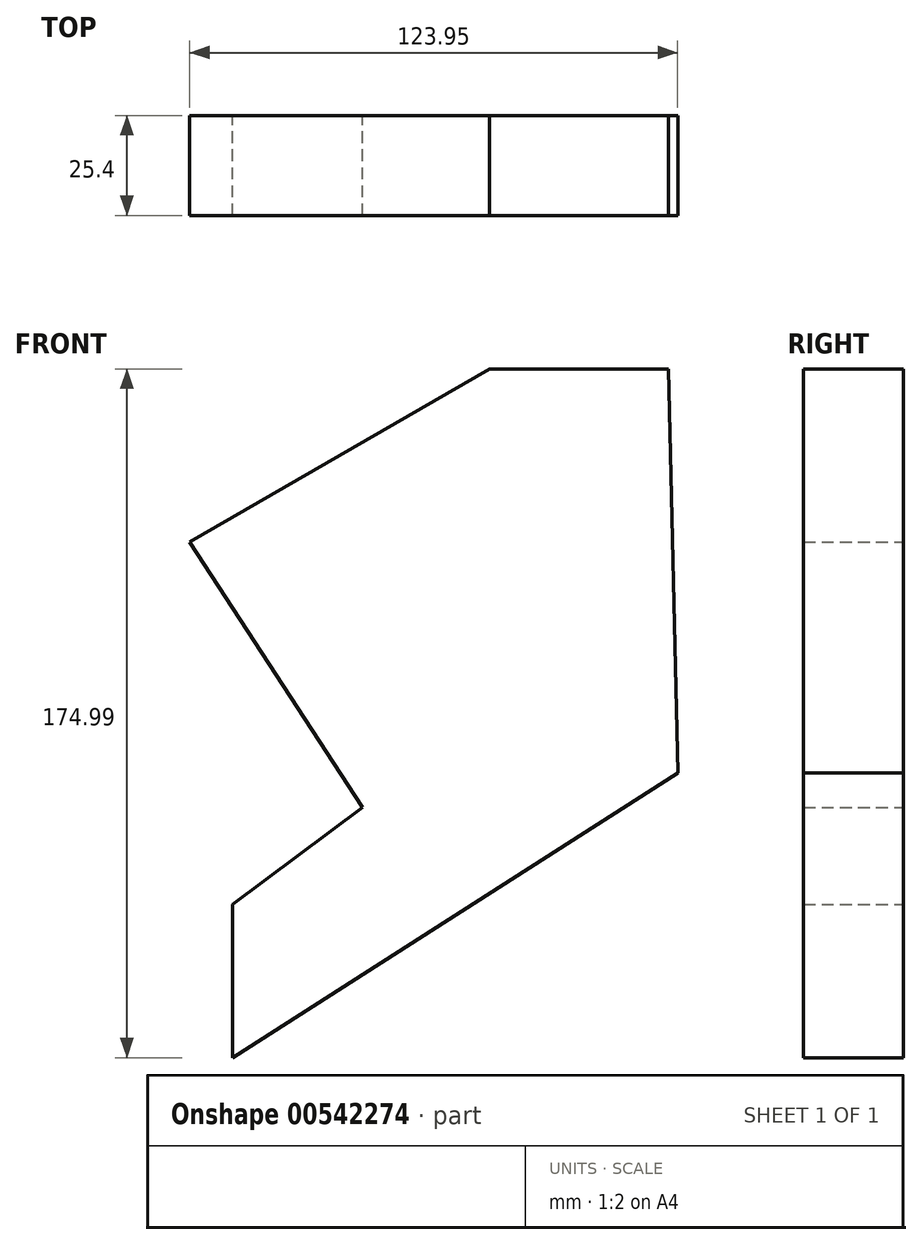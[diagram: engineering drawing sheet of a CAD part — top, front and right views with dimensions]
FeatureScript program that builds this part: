
annotation { "Feature Type Name" : "Feature", "Feature Type Description" : "" }
export const myFeature = defineFeature(function(context is Context, id is Id, definition is map)
    precondition{}
    {
        {
            var Q0;
            Q0=qCreatedBy(makeId("Front.planeOp"),FACE);
            var sketch = newSketch(context, id + "F0", { "sketchPlane" : qUnion([Q0])});
            skLineSegment(sketch, "E0", {"start": v(-15.58, -15.97) * mm, "end": v(-59.47, 51.43) * mm});
            skLineSegment(sketch, "E1", {"start": v(-59.47, 51.43) * mm, "end": v(16.73, 95.42) * mm});
            skLineSegment(sketch, "E2", {"start": v(16.73, 95.42) * mm, "end": v(62.13, 95.42) * mm});
            skLineSegment(sketch, "E3", {"start": v(62.13, 95.42) * mm, "end": v(64.48, -7.25) * mm});
            skLineSegment(sketch, "E4", {"start": v(64.48, -7.25) * mm, "end": v(-48.59, -79.57) * mm});
            skLineSegment(sketch, "E5", {"start": v(-48.59, -79.57) * mm, "end": v(-48.59, -40.65) * mm});
            skLineSegment(sketch, "E6", {"start": v(-48.59, -40.65) * mm, "end": v(-15.58, -15.97) * mm});
            skSolve(sketch);
        }
        {
            var Q0;
            Q0=makeQuery(id+"F0.imprint","IMPRINT",FACE,{"disambiguationData":[TD([[makeQuery(id+"F0.imprint","IMPRINT",EDGE,{"derivedFrom":sQuery(id+"F0.wireOp",EDGE,"E0")}),-1.0]])]});
            extrude(context, id + "F1", {"entities" : qUnion([Q0]), "depth" : 25.4 * mm, "offsetDistance" : 25.4 * mm});
        }
    });
